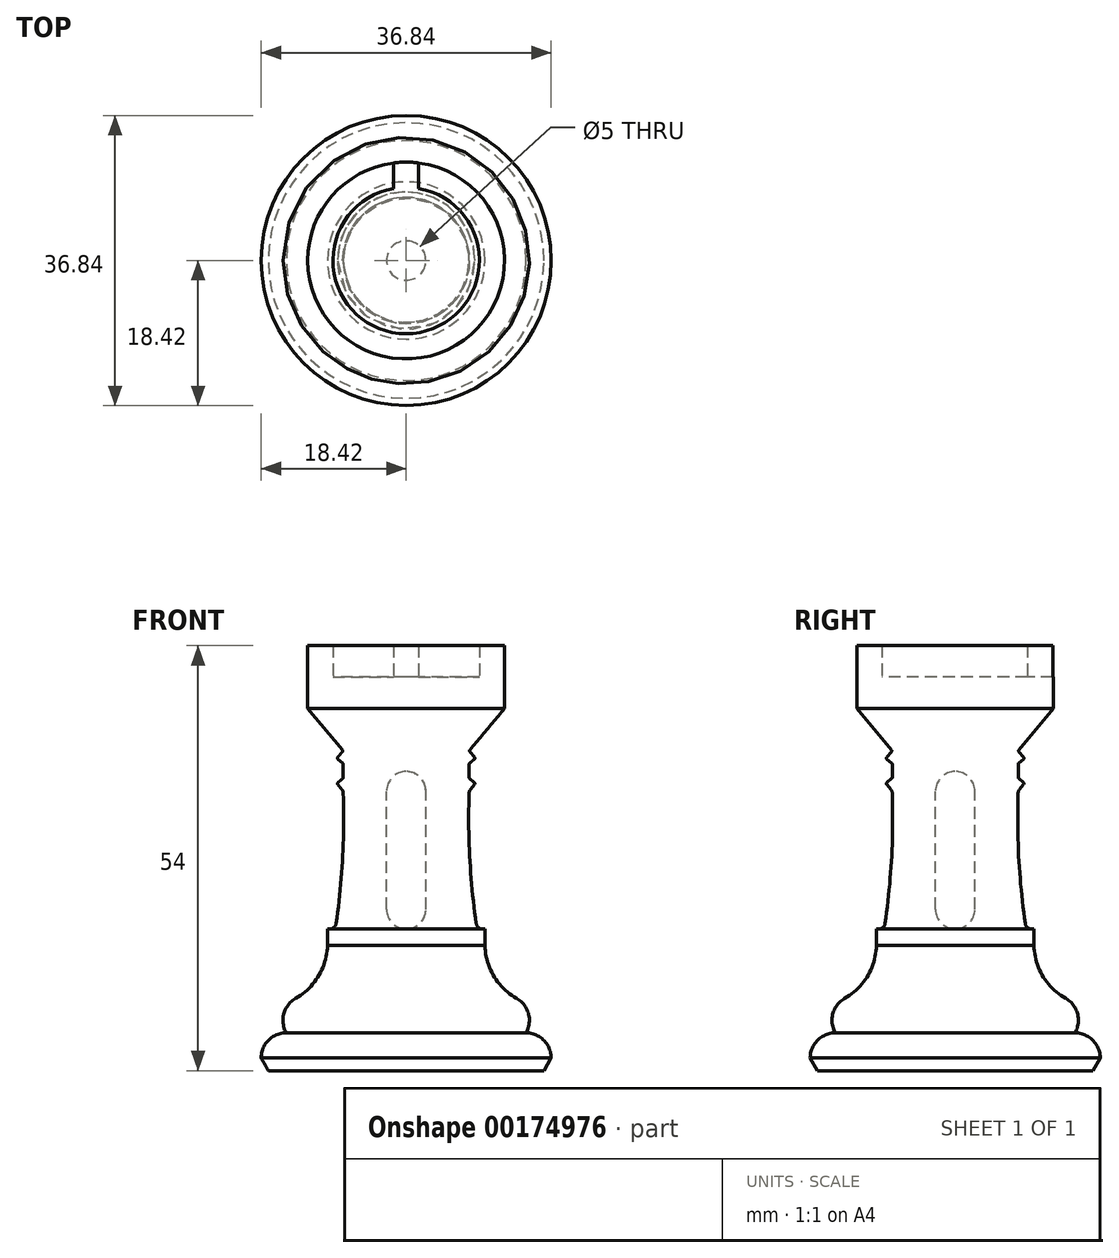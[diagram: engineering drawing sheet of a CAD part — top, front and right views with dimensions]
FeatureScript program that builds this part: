
annotation { "Feature Type Name" : "Feature", "Feature Type Description" : "" }
export const myFeature = defineFeature(function(context is Context, id is Id, definition is map)
    precondition{}
    {
        {
            var Q0;
            Q0=qCreatedBy(makeId("Front.planeOp"),FACE);
            var sketch = newSketch(context, id + "F0", { "sketchPlane" : qUnion([Q0])});
            skLineSegment(sketch, "E0", {"start": v(0, 0) * mm, "end": v(17.5, 0) * mm});
            skLineSegment(sketch, "E1", {"start": v(0, 0) * mm, "end": v(0, 95) * mm, "construction": true});
            skLineSegment(sketch, "E2", {"start": v(0, 18) * mm, "end": v(10, 18) * mm, "construction": true});
            skLineSegment(sketch, "E3", {"start": v(14.4, 35) * mm, "end": v(0, 35) * mm, "construction": true});
            skLineSegment(sketch, "E4", {"start": v(0, 48.6) * mm, "end": v(12.7, 48.6) * mm, "construction": true});
            skLineSegment(sketch, "E5", {"start": v(0, 64.34) * mm, "end": v(14.8, 64.34) * mm, "construction": true});
            skLineSegment(sketch, "E6", {"start": v(17.5, 0) * mm, "end": v(18.42, 1.6) * mm});
            skArc(sketch, "E7", {"start": v(18.42, 1.6) * mm, "mid": v(17.49, 3.86) * mm, "end": v(15.22, 4.8) * mm});
            skLineSegment(sketch, "E8", {"start": v(10, 18) * mm, "end": v(10, 15.92) * mm});
            skArc(sketch, "E9", {"start": v(10, 15.92) * mm, "mid": v(11.13, 12.02) * mm, "end": v(14.04, 9.18) * mm});
            skArc(sketch, "E10", {"start": v(15.22, 4.8) * mm, "mid": v(15.54, 7.24) * mm, "end": v(14.04, 9.18) * mm});
            skLineSegment(sketch, "E11", {"start": v(10, 18) * mm, "end": v(9, 18) * mm});
            skArc(sketch, "E12", {"start": v(8, 35.53) * mm, "mid": v(8.1, 26.74) * mm, "end": v(9, 18) * mm});
            skLineSegment(sketch, "E13", {"start": v(8, 35.53) * mm, "end": v(8.8, 36.48) * mm});
            skLineSegment(sketch, "E14", {"start": v(8.8, 36.48) * mm, "end": v(8, 37.15) * mm});
            skLineSegment(sketch, "E15", {"start": v(8, 37.15) * mm, "end": v(8, 39.01) * mm});
            skLineSegment(sketch, "E16", {"start": v(8, 39.01) * mm, "end": v(8.8, 39.68) * mm});
            skLineSegment(sketch, "E17", {"start": v(8.8, 39.68) * mm, "end": v(8, 40.64) * mm});
            skLineSegment(sketch, "E18", {"start": v(3.2, 50) * mm, "end": v(0, 50) * mm});
            skLineSegment(sketch, "E19", {"start": v(0, 50) * mm, "end": v(0, 0) * mm});
            skLineSegment(sketch, "E20", {"start": v(3.2, 50) * mm, "end": v(9.3, 50) * mm});
            skLineSegment(sketch, "E21", {"start": v(9.3, 50) * mm, "end": v(9.3, 54) * mm});
            skLineSegment(sketch, "E22", {"start": v(9.3, 54) * mm, "end": v(12.5, 54) * mm});
            skLineSegment(sketch, "E23", {"start": v(12.5, 54) * mm, "end": v(12.5, 46) * mm});
            skLineSegment(sketch, "E24", {"start": v(8, 40.64) * mm, "end": v(12.5, 46) * mm});
            skSolve(sketch);
        }
        {
            var Q0;
            Q0=qSketchRegion(id+"F0",true);
            var Q1;
            Q1=sQuery(id+"F0.wireOp",EDGE,"E1");
            revolve(context, id + "F1", {"entities" : qUnion([Q0]), "axis" : qUnion([Q1]), "revolveType" : RevolveType.FULL});
        }
        {
            var Q0;
            Q0=makeQuery(id+"F1.opRevolve","SWEPT_EDGE",EDGE,{"disambiguationData":[OSD([sQuery(id+"F0.wireOp",EDGE,"E12"),sQuery(id+"F0.wireOp",EDGE,"0I6bwwmy-hoyF-qGjU-uGXw-rzDxYN856Fuf")])]});
            var Q1;
            Q1=makeQuery(id+"F1.opRevolve","SWEPT_EDGE",EDGE,{"disambiguationData":[OSD([sQuery(id+"F0.wireOp",EDGE,"E11"),sQuery(id+"F0.wireOp",EDGE,"E12")])]});
            fillet(context, id + "F2", {"entities" : qUnion([Q0, Q1]), "radius" : .8 * mm, "tangentPropagation" : true, "allowEdgeOverflow" : false});
        }
        {
            var Q0;
            Q0=makeQuery(id+"F1.opRevolve","SWEPT_EDGE",EDGE,{"disambiguationData":[OSD([sQuery(id+"F0.wireOp",EDGE,"E16"),sQuery(id+"F0.wireOp",EDGE,"E17")])]});
            var Q1;
            Q1=makeQuery(id+"F1.opRevolve","SWEPT_EDGE",EDGE,{"disambiguationData":[OSD([sQuery(id+"F0.wireOp",EDGE,"E13"),sQuery(id+"F0.wireOp",EDGE,"E14")])]});
            var Q2;
            Q2=makeQuery(id+"F1.opRevolve","SWEPT_EDGE",EDGE,{"disambiguationData":[OSD([sQuery(id+"F0.wireOp",EDGE,"OAx1KunF-KjKq-zgV9-Glhn-Sdbq04AqaJ7j"),sQuery(id+"F0.wireOp",EDGE,"E17")])]});
            var Q3;
            Q3=makeQuery(id+"F1.opRevolve","SWEPT_EDGE",EDGE,{"disambiguationData":[OSD([sQuery(id+"F0.wireOp",EDGE,"E15"),sQuery(id+"F0.wireOp",EDGE,"E16")])]});
            var Q4;
            Q4=makeQuery(id+"F1.opRevolve","SWEPT_EDGE",EDGE,{"disambiguationData":[OSD([sQuery(id+"F0.wireOp",EDGE,"E14"),sQuery(id+"F0.wireOp",EDGE,"E15")])]});
            var Q5;
            Q5=makeQuery(id+"F1.opRevolve","SWEPT_EDGE",EDGE,{"disambiguationData":[OSD([sQuery(id+"F0.wireOp",EDGE,"0I6bwwmy-hoyF-qGjU-uGXw-rzDxYN856Fuf"),sQuery(id+"F0.wireOp",EDGE,"E13")])]});
            fillet(context, id + "F3", {"entities" : qUnion([Q0, Q1, Q2, Q3, Q4, Q5]), "radius" : .2 * mm, "tangentPropagation" : true, "allowEdgeOverflow" : false});
        }
        {
            var Q0;
            Q0=qCreatedBy(makeId("Front.planeOp"),FACE);
            var sketch = newSketch(context, id + "F4", { "sketchPlane" : qUnion([Q0])});
            skLineSegment(sketch, "E25.bottom", {"start": v(0, 18) * mm, "end": v(0, 18) * mm});
            skLineSegment(sketch, "E25.top", {"start": v(0, 38) * mm, "end": v(0, 38) * mm});
            skLineSegment(sketch, "E25.left", {"start": v(2.5, 20.5) * mm, "end": v(2.5, 35.5) * mm});
            skPoint(sketch, "E25.middle", {"position": v(0, 28) * mm});
            skPoint(sketch, "E26.visualSharp", {"position": v(2.5, 38) * mm});
            skArc(sketch, "E26.filletArc", {"start": v(2.5, 35.5) * mm, "mid": v(1.77, 37.27) * mm, "end": v(0, 38) * mm});
            skPoint(sketch, "E27.visualSharp", {"position": v(-2.5, 38) * mm});
            skPoint(sketch, "E28.visualSharp", {"position": v(-2.5, 18) * mm});
            skPoint(sketch, "E29.visualSharp", {"position": v(2.5, 18) * mm});
            skArc(sketch, "E29.filletArc", {"start": v(0, 18) * mm, "mid": v(1.77, 18.73) * mm, "end": v(2.5, 20.5) * mm});
            skLineSegment(sketch, "E30", {"start": v(0, 38) * mm, "end": v(0, 18) * mm});
            skSolve(sketch);
        }
        {
            var Q0;
            Q0=qSketchRegion(id+"F4",true);
            var Q1;
            Q1=qConstructionFilter(qBodyType(qCreatedBy(id+"F4",EDGE),BodyType.WIRE),ConstructionObject.NO);
            var Q2;
            Q2=sQuery(id+"F4.wireOp",EDGE,"E30");
            revolve(context, id + "F5", {"operationType" : NewBodyOperationType.REMOVE, "entities" : qUnion([Q0]), "surfaceEntities" : qUnion([Q1]), "axis" : qUnion([Q2]), "revolveType" : RevolveType.FULL});
        }
        {
            var Q0;
            Q0=qCreatedBy(makeId("Front.planeOp"),FACE);
            var sketch = newSketch(context, id + "F6", { "sketchPlane" : qUnion([Q0])});
            skLineSegment(sketch, "E31.bottom", {"start": v(1.6, 50) * mm, "end": v(-1.6, 50) * mm});
            skLineSegment(sketch, "E31.top", {"start": v(1.6, 54) * mm, "end": v(-1.6, 54) * mm});
            skLineSegment(sketch, "E31.left", {"start": v(1.6, 50) * mm, "end": v(1.6, 54) * mm});
            skLineSegment(sketch, "E31.right", {"start": v(-1.6, 50) * mm, "end": v(-1.6, 54) * mm});
            skPoint(sketch, "E31.middle", {"position": v(0, 52) * mm});
            skSolve(sketch);
        }
        {
            var Q0;
            Q0 = qSketchRegion(id + "F6", true);
            extrude(context, id + "F7", {"entities" : qUnion([Q0]), "operationType" : NewBodyOperationType.REMOVE, "oppositeDirection" : true, "depth" : 25 * mm});
        }
    });
